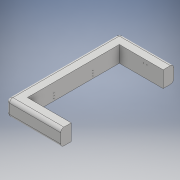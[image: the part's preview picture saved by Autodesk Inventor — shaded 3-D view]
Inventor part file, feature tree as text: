
AUTODESK INVENTOR PART (.ipt)
format: ipt  version: 2018 (Build 220112000, 112)  size: 164,864 bytes
history: native  units: in
note: dims shown in document units (in); Inventor stores cm internally (conversion verified against a paired STEP export)
features: extrude x4, sketch x4, fillet x1
ambient origin geometry x8: Origin, YZ Plane, XZ Plane, XY Plane, X Axis, Y Axis, Z Axis, Center Point
bodies: Solid1 (feature_tree)
feature tree (9):
  extrude  "Extrusion1"  Depth=13.5in
  fillet  "Fillet1"  Radius=3.25in
  sketch  "Sketch2"  dims[d3=5.0in d4=0.0in d5=1.0in]
  sketch  "Sketch3"  dims[d23=8.155in d24=2.83in]
  extrude  "Extrusion4"  Depth=1.0in
  extrude  "Extrusion5"  Depth=2.83in
  extrude  "Extrusion6"  Depth=1.0in
  sketch  "Sketch1"  dims[d0=28.31in d1=13.5in d2=3.25in]
  sketch  "Sketch4"  dims[d25=0.75in d26=0.75in d27=0.21in d28=0.1875in d29=0.0in d30=7.5in d31=3.83in d32=90.0deg d33=1.0in d34=0.2031in d35=1.0in d36=0.0in d37=7.5in d38=1.17in d39=90.0deg d40=1.0in d41=0.0in d42=0.2031in d43=1.0in d44=0.0in]
